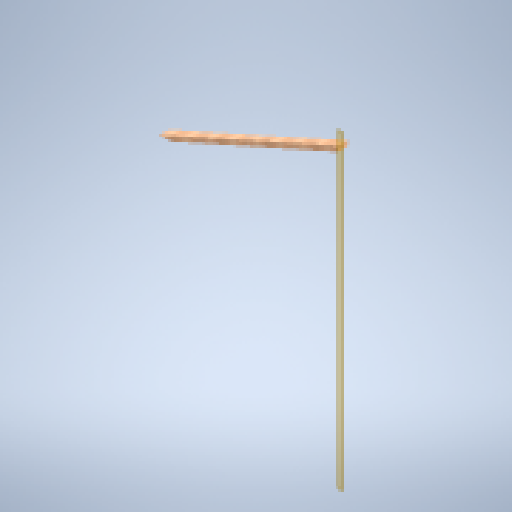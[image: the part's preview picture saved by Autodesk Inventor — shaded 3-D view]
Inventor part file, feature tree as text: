
AUTODESK INVENTOR PART (.ipt)
format: ipt  version: 2025 (Build 290162000, 162)  size: 141,824 bytes
history: native  units: in
note: dims shown in document units (in); Inventor stores cm internally (conversion verified against a paired STEP export)
features: other x5, reference x3, plane x2, extrude x1, sketch x1
ambient origin geometry x8: Origin, YZ Plane, XZ Plane, XY Plane, X Axis, Y Axis, Z Axis, Center Point
bodies: Body1 (feature_tree)
feature tree (12):
  plane  "Work Plane1"
  plane  "Work Plane2"
  extrude  "Extrusion2"  Depth=4.0in TaperAngle=0.0deg
  sketch  "Sketch2"  dims[d1=2.0in d4=4.0in d5=0.0in]
  reference  "Reference3"
  reference  "Reference4"
  reference  "Reference5"
  other  "<userpath>\Documents\GitHub\USCTigerBurn24\v2\Tiger.iam"
  other  "Tiger.iam"
  other  "2x4x48:11"
  other  "2x4x72:7"
  other  "2x4x120:6"
